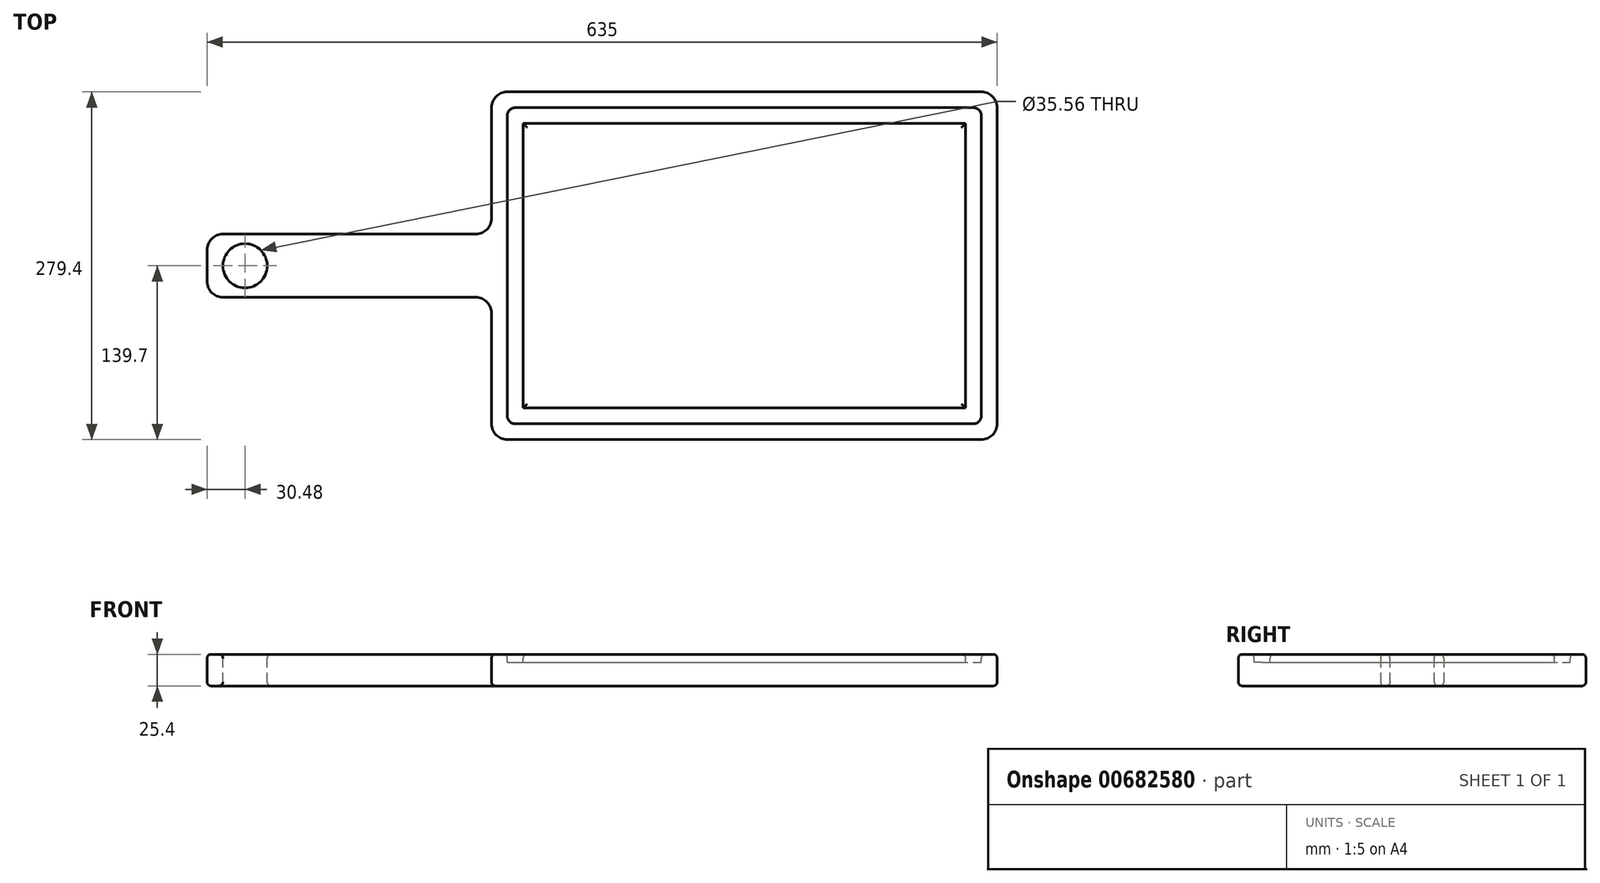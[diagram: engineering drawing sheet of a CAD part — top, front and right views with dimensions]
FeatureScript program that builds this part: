
annotation { "Feature Type Name" : "Feature", "Feature Type Description" : "" }
export const myFeature = defineFeature(function(context is Context, id is Id, definition is map)
    precondition{}
    {
        {
            var Q0;
            Q0=qCreatedBy(makeId("Top.planeOp"),FACE);
            var sketch = newSketch(context, id + "F0", { "sketchPlane" : qUnion([Q0])});
            skLineSegment(sketch, "E0.bottom", {"start": v(0, 0) * mm, "end": v(406.4, 0) * mm});
            skLineSegment(sketch, "E0.top", {"start": v(0, 279.4) * mm, "end": v(406.4, 279.4) * mm});
            skLineSegment(sketch, "E0.left", {"start": v(0, 0) * mm, "end": v(0, 279.4) * mm});
            skLineSegment(sketch, "E0.right", {"start": v(406.4, 0) * mm, "end": v(406.4, 279.4) * mm});
            skLineSegment(sketch, "E1.bottom", {"start": v(-228.6, 165.1) * mm, "end": v(0, 165.1) * mm});
            skLineSegment(sketch, "E1.top", {"start": v(-228.6, 114.3) * mm, "end": v(0, 114.3) * mm});
            skLineSegment(sketch, "E1.left", {"start": v(-228.6, 165.1) * mm, "end": v(-228.6, 114.3) * mm});
            skLineSegment(sketch, "E1.right", {"start": v(0, 165.1) * mm, "end": v(0, 114.3) * mm});
            skSolve(sketch);
        }
        {
            var Q0;
            Q0=makeQuery(id+"F0.imprint","IMPRINT",FACE,{"disambiguationData":[TD([[makeQuery(id+"F0.imprint","IMPRINT",EDGE,{"derivedFrom":sQuery(id+"F0.wireOp",EDGE,"E1.bottom")}),-1.0]])]});
            var Q1;
            {var subQ3=sQuery(id+"F0.wireOp",EDGE,"E0.bottom");Q1=makeQuery(id+"F0.imprint","IMPRINT",FACE,{"disambiguationData":[TD([[makeQuery(id+"F0.imprint","IMPRINT",EDGE,{"derivedFrom":subQ3}),1.0]])]});}
            extrude(context, id + "F1", {"entities" : qUnion([Q0, Q1]), "depth" : 25.4 * mm, "offsetDistance" : 25.4 * mm});
        }
        {
            var Q0;
            Q0=makeQuery(id+"F1.opExtrude","CAP_FACE",FACE,{"disambiguationData":[OSD([sQuery(id+"F0.wireOp",EDGE,"E0.bottom"),sQuery(id+"F0.wireOp",EDGE,"E0.top"),sQuery(id+"F0.wireOp",EDGE,"E0.left"),sQuery(id+"F0.wireOp",EDGE,"E0.right"),sQuery(id+"F0.wireOp",EDGE,"E1.bottom"),sQuery(id+"F0.wireOp",EDGE,"E1.top"),sQuery(id+"F0.wireOp",EDGE,"E1.left")])],"isStart":false});
            var sketch = newSketch(context, id + "F2", { "sketchPlane" : qUnion([Q0])});
            skCircle(sketch, "E2", {"center": v(-198.12, 139.7) * mm, "radius": 17.78 * mm});
            skSolve(sketch);
        }
        {
            var Q0;
            Q0 = qSketchRegion(id + "F0", true);
            extrude(context, id + "F3", {"entities" : qUnion([Q0]), "operationType" : NewBodyOperationType.ADD, "depth" : 25.4 * mm, "offsetDistance" : 25.4 * mm});
        }
        {
            var Q0;
            Q0 = qSketchRegion(id + "F2", true);
            extrude(context, id + "F4", {"entities" : qUnion([Q0]), "operationType" : NewBodyOperationType.REMOVE, "oppositeDirection" : true, "depth" : 25.4 * mm, "offsetDistance" : 25.4 * mm});
        }
        {
            var Q0;
            Q0=makeQuery(id+"F1.opExtrude","CAP_FACE",FACE,{"disambiguationData":[OSD([sQuery(id+"F0.wireOp",EDGE,"E0.bottom"),sQuery(id+"F0.wireOp",EDGE,"E0.top"),sQuery(id+"F0.wireOp",EDGE,"E0.left"),sQuery(id+"F0.wireOp",EDGE,"E0.right"),sQuery(id+"F0.wireOp",EDGE,"E1.bottom"),sQuery(id+"F0.wireOp",EDGE,"E1.top"),sQuery(id+"F0.wireOp",EDGE,"E1.left")])],"isStart":false});
            var sketch = newSketch(context, id + "F5", { "sketchPlane" : qUnion([Q0])});
            skLineSegment(sketch, "E3.0", {"start": v(12.7, 12.7) * mm, "end": v(12.7, 114.3) * mm});
            skLineSegment(sketch, "E3.1", {"start": v(12.7, 165.1) * mm, "end": v(12.7, 266.7) * mm});
            skLineSegment(sketch, "E3.2", {"start": v(12.7, 266.7) * mm, "end": v(393.7, 266.7) * mm});
            skLineSegment(sketch, "E3.3", {"start": v(393.7, 12.7) * mm, "end": v(393.7, 266.7) * mm});
            skLineSegment(sketch, "E3.4", {"start": v(12.7, 12.7) * mm, "end": v(393.7, 12.7) * mm});
            skLineSegment(sketch, "E4", {"start": v(12.7, 165.1) * mm, "end": v(12.7, 114.3) * mm});
            skLineSegment(sketch, "E5.0", {"start": v(25.4, 165.1) * mm, "end": v(25.4, 254) * mm});
            skLineSegment(sketch, "E5.1", {"start": v(381, 25.4) * mm, "end": v(381, 254) * mm});
            skLineSegment(sketch, "E5.2", {"start": v(25.4, 25.4) * mm, "end": v(381, 25.4) * mm});
            skLineSegment(sketch, "E5.3", {"start": v(25.4, 254) * mm, "end": v(381, 254) * mm});
            skLineSegment(sketch, "E5.4", {"start": v(25.4, 25.4) * mm, "end": v(25.4, 114.3) * mm});
            skLineSegment(sketch, "E5.5", {"start": v(25.4, 165.1) * mm, "end": v(25.4, 114.3) * mm});
            skSolve(sketch);
        }
        {
            var Q0;
            Q0=makeQuery(id+"F5.imprint","IMPRINT",FACE,{"disambiguationData":[TD([[makeQuery(id+"F5.imprint","IMPRINT",EDGE,{"derivedFrom":sQuery(id+"F5.wireOp",EDGE,"E3.0")}),-1.0]])]});
            extrude(context, id + "F6", {"entities" : qUnion([Q0]), "operationType" : NewBodyOperationType.REMOVE, "oppositeDirection" : true, "depth" : 6.35 * mm, "offsetDistance" : 25.4 * mm});
        }
        {
            var Q0;
            Q0=makeQuery(id+"F6.boolean.opBoolean","COPY",EDGE,{"derivedFrom":makeQuery(id+"F6.opExtrude","SWEPT_EDGE",EDGE,{"disambiguationData":[OSD([sQuery(id+"F5.wireOp",EDGE,"E3.1"),sQuery(id+"F5.wireOp",EDGE,"E3.2")])]})});
            var Q1;
            Q1=makeQuery(id+"F6.boolean.opBoolean","COPY",EDGE,{"derivedFrom":makeQuery(id+"F6.opExtrude","SWEPT_EDGE",EDGE,{"disambiguationData":[OSD([sQuery(id+"F5.wireOp",EDGE,"E3.2"),sQuery(id+"F5.wireOp",EDGE,"E3.3")])]})});
            var Q2;
            Q2=makeQuery(id+"F6.boolean.opBoolean","COPY",EDGE,{"derivedFrom":makeQuery(id+"F6.opExtrude","SWEPT_EDGE",EDGE,{"disambiguationData":[OSD([sQuery(id+"F5.wireOp",EDGE,"E3.3"),sQuery(id+"F5.wireOp",EDGE,"E3.4")])]})});
            var Q3;
            Q3=makeQuery(id+"F6.boolean.opBoolean","COPY",EDGE,{"derivedFrom":makeQuery(id+"F6.opExtrude","SWEPT_EDGE",EDGE,{"disambiguationData":[OSD([sQuery(id+"F5.wireOp",EDGE,"E3.0"),sQuery(id+"F5.wireOp",EDGE,"E3.4")])]})});
            fillet(context, id + "F7", {"entities" : qUnion([Q0, Q1, Q2, Q3]), "radius" : 6.35 * mm, "tangentPropagation" : true, "allowEdgeOverflow" : false});
        }
        {
            var Q0;
            Q0=makeQuery(id+"F1.opExtrude","SWEPT_EDGE",EDGE,{"disambiguationData":[OSD([sQuery(id+"F0.wireOp",EDGE,"E0.bottom"),sQuery(id+"F0.wireOp",EDGE,"E0.left")])]});
            var Q1;
            Q1=makeQuery(id+"F1.opExtrude","SWEPT_EDGE",EDGE,{"disambiguationData":[OSD([sQuery(id+"F0.wireOp",EDGE,"E0.top"),sQuery(id+"F0.wireOp",EDGE,"E0.left")])]});
            var Q2;
            Q2=makeQuery(id+"F1.opExtrude","SWEPT_EDGE",EDGE,{"disambiguationData":[OSD([sQuery(id+"F0.wireOp",EDGE,"E0.top"),sQuery(id+"F0.wireOp",EDGE,"E0.right")])]});
            var Q3;
            Q3=makeQuery(id+"F1.opExtrude","SWEPT_EDGE",EDGE,{"disambiguationData":[OSD([sQuery(id+"F0.wireOp",EDGE,"E0.bottom"),sQuery(id+"F0.wireOp",EDGE,"E0.right")])]});
            var Q4;
            Q4=makeQuery(id+"F1.opExtrude","SWEPT_EDGE",EDGE,{"disambiguationData":[OSD([sQuery(id+"F0.wireOp",EDGE,"E1.top"),sQuery(id+"F0.wireOp",EDGE,"E1.left")])]});
            var Q5;
            Q5=makeQuery(id+"F1.opExtrude","SWEPT_EDGE",EDGE,{"disambiguationData":[OSD([sQuery(id+"F0.wireOp",EDGE,"E1.bottom"),sQuery(id+"F0.wireOp",EDGE,"E1.left")])]});
            var Q6;
            Q6=makeQuery(id+"F1.opExtrude","SWEPT_EDGE",EDGE,{"disambiguationData":[OSD([sQuery(id+"F0.wireOp",EDGE,"E0.left"),sQuery(id+"F0.wireOp",EDGE,"E1.bottom"),sQuery(id+"F0.wireOp",EDGE,"E1.right")])]});
            var Q7;
            Q7=makeQuery(id+"F1.opExtrude","SWEPT_EDGE",EDGE,{"disambiguationData":[OSD([sQuery(id+"F0.wireOp",EDGE,"E0.left"),sQuery(id+"F0.wireOp",EDGE,"E1.top"),sQuery(id+"F0.wireOp",EDGE,"E1.right")])]});
            fillet(context, id + "F8", {"entities" : qUnion([Q0, Q1, Q2, Q3, Q4, Q5, Q6, Q7]), "radius" : 12.7 * mm, "tangentPropagation" : true, "allowEdgeOverflow" : false});
        }
        {
            var Q0;
            Q0=makeQuery(id+"F6.boolean.opBoolean","SPLIT",FACE,{"disambiguationData":[TD([makeQuery(id+"F6.opExtrude","SWEPT_FACE",FACE,{"disambiguationData":[OSD([sQuery(id+"F5.wireOp",EDGE,"E5.1")])]})])],"derivedFrom":makeQuery(id+"F1.opExtrude","CAP_FACE",FACE,{"disambiguationData":[OSD([sQuery(id+"F0.wireOp",EDGE,"E0.bottom"),sQuery(id+"F0.wireOp",EDGE,"E0.top"),sQuery(id+"F0.wireOp",EDGE,"E0.left"),sQuery(id+"F0.wireOp",EDGE,"E0.right"),sQuery(id+"F0.wireOp",EDGE,"E1.bottom"),sQuery(id+"F0.wireOp",EDGE,"E1.top"),sQuery(id+"F0.wireOp",EDGE,"E1.left")])],"isStart":false})});
            var Q1;
            {var subQ0=sQuery(id+"F0.wireOp",EDGE,"E1.left");var subQ1=sQuery(id+"F0.wireOp",EDGE,"E1.top");var subQ2=sQuery(id+"F0.wireOp",EDGE,"E1.bottom");var subQ3=sQuery(id+"F0.wireOp",EDGE,"E0.right");var subQ4=sQuery(id+"F0.wireOp",EDGE,"E0.bottom");var subQ5=sQuery(id+"F0.wireOp",EDGE,"E0.left");var subQ6=sQuery(id+"F0.wireOp",EDGE,"E0.top");Q1=makeQuery(id+"F6.boolean.opBoolean","SPLIT",FACE,{"disambiguationData":[TD([makeQuery(id+"F1.opExtrude","SWEPT_FACE",FACE,{"disambiguationData":[OSD([subQ4])]})])],"derivedFrom":makeQuery(id+"F1.opExtrude","CAP_FACE",FACE,{"disambiguationData":[OSD([subQ4,subQ6,subQ5,subQ3,subQ2,subQ1,subQ0])],"isStart":false})});}
            var Q2;
            Q2=makeQuery(id+"F1.opExtrude","CAP_FACE",FACE,{"disambiguationData":[OSD([sQuery(id+"F0.wireOp",EDGE,"E0.bottom"),sQuery(id+"F0.wireOp",EDGE,"E0.top"),sQuery(id+"F0.wireOp",EDGE,"E0.left"),sQuery(id+"F0.wireOp",EDGE,"E0.right"),sQuery(id+"F0.wireOp",EDGE,"E1.bottom"),sQuery(id+"F0.wireOp",EDGE,"E1.top"),sQuery(id+"F0.wireOp",EDGE,"E1.left")])],"isStart":true});
            fillet(context, id + "F9", {"entities" : qUnion([Q0, Q1, Q2]), "radius" : 3.17 * mm, "tangentPropagation" : true, "allowEdgeOverflow" : false});
        }
    });
